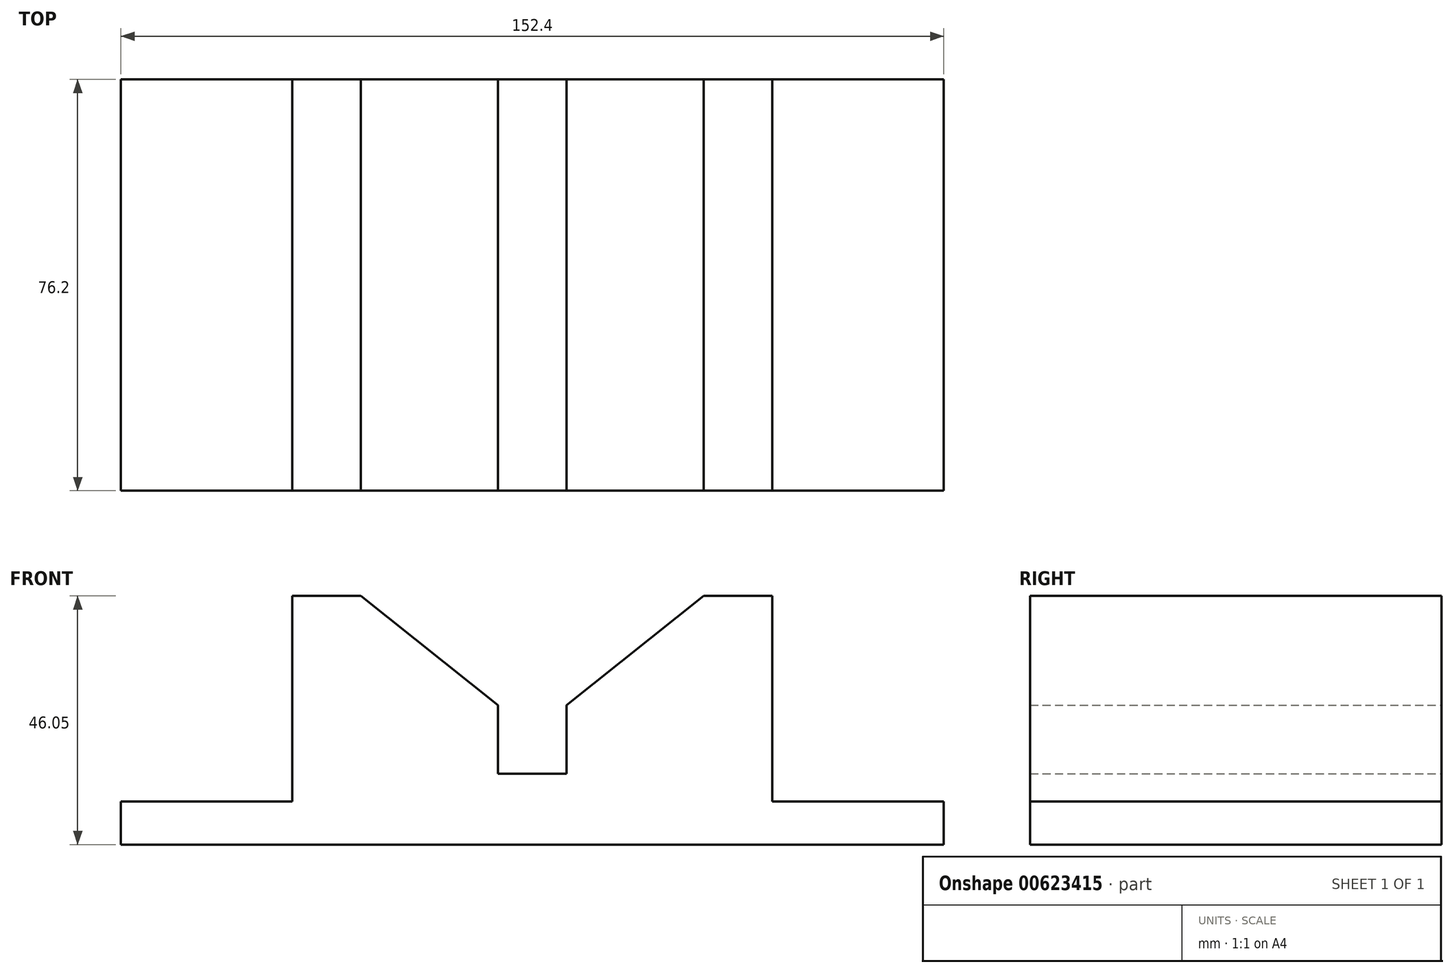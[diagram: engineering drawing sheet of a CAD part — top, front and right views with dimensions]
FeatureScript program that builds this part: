
annotation { "Feature Type Name" : "Feature", "Feature Type Description" : "" }
export const myFeature = defineFeature(function(context is Context, id is Id, definition is map)
    precondition{}
    {
        {
            var Q0;
            Q0=qCreatedBy(makeId("Front.planeOp"),FACE);
            var sketch = newSketch(context, id + "F0", { "sketchPlane" : qUnion([Q0])});
            skLineSegment(sketch, "E0", {"start": v(-49.9, -70.1) * mm, "end": v(102.5, -70.1) * mm});
            skLineSegment(sketch, "E1", {"start": v(102.5, -70.1) * mm, "end": v(102.5, -62.16) * mm});
            skLineSegment(sketch, "E2", {"start": v(102.5, -62.16) * mm, "end": v(70.74, -62.16) * mm});
            skLineSegment(sketch, "E3", {"start": v(70.74, -62.16) * mm, "end": v(70.74, -24.06) * mm});
            skLineSegment(sketch, "E4", {"start": v(70.74, -24.06) * mm, "end": v(58.04, -24.06) * mm});
            skLineSegment(sketch, "E5", {"start": v(58.04, -24.06) * mm, "end": v(32.64, -44.27) * mm});
            skLineSegment(sketch, "E6", {"start": v(32.64, -44.27) * mm, "end": v(32.64, -56.97) * mm});
            skLineSegment(sketch, "E7", {"start": v(32.64, -56.97) * mm, "end": v(19.94, -56.97) * mm});
            skLineSegment(sketch, "E8", {"start": v(19.94, -56.97) * mm, "end": v(19.94, -44.27) * mm});
            skLineSegment(sketch, "E9", {"start": v(19.94, -44.27) * mm, "end": v(-5.46, -24.06) * mm});
            skLineSegment(sketch, "E10", {"start": v(-5.46, -24.06) * mm, "end": v(-18.16, -24.06) * mm});
            skLineSegment(sketch, "E11", {"start": v(-18.16, -24.06) * mm, "end": v(-18.16, -62.16) * mm});
            skLineSegment(sketch, "E12", {"start": v(-18.16, -62.16) * mm, "end": v(-49.9, -62.16) * mm});
            skLineSegment(sketch, "E13", {"start": v(-49.9, -62.16) * mm, "end": v(-49.9, -70.1) * mm});
            skSolve(sketch);
        }
        {
            var Q0;
            Q0 = qSketchRegion(id + "F0", true);
            extrude(context, id + "F1", {"entities" : qUnion([Q0]), "depth" : 76.2 * mm, "offsetDistance" : 25.4 * mm});
        }
    });
